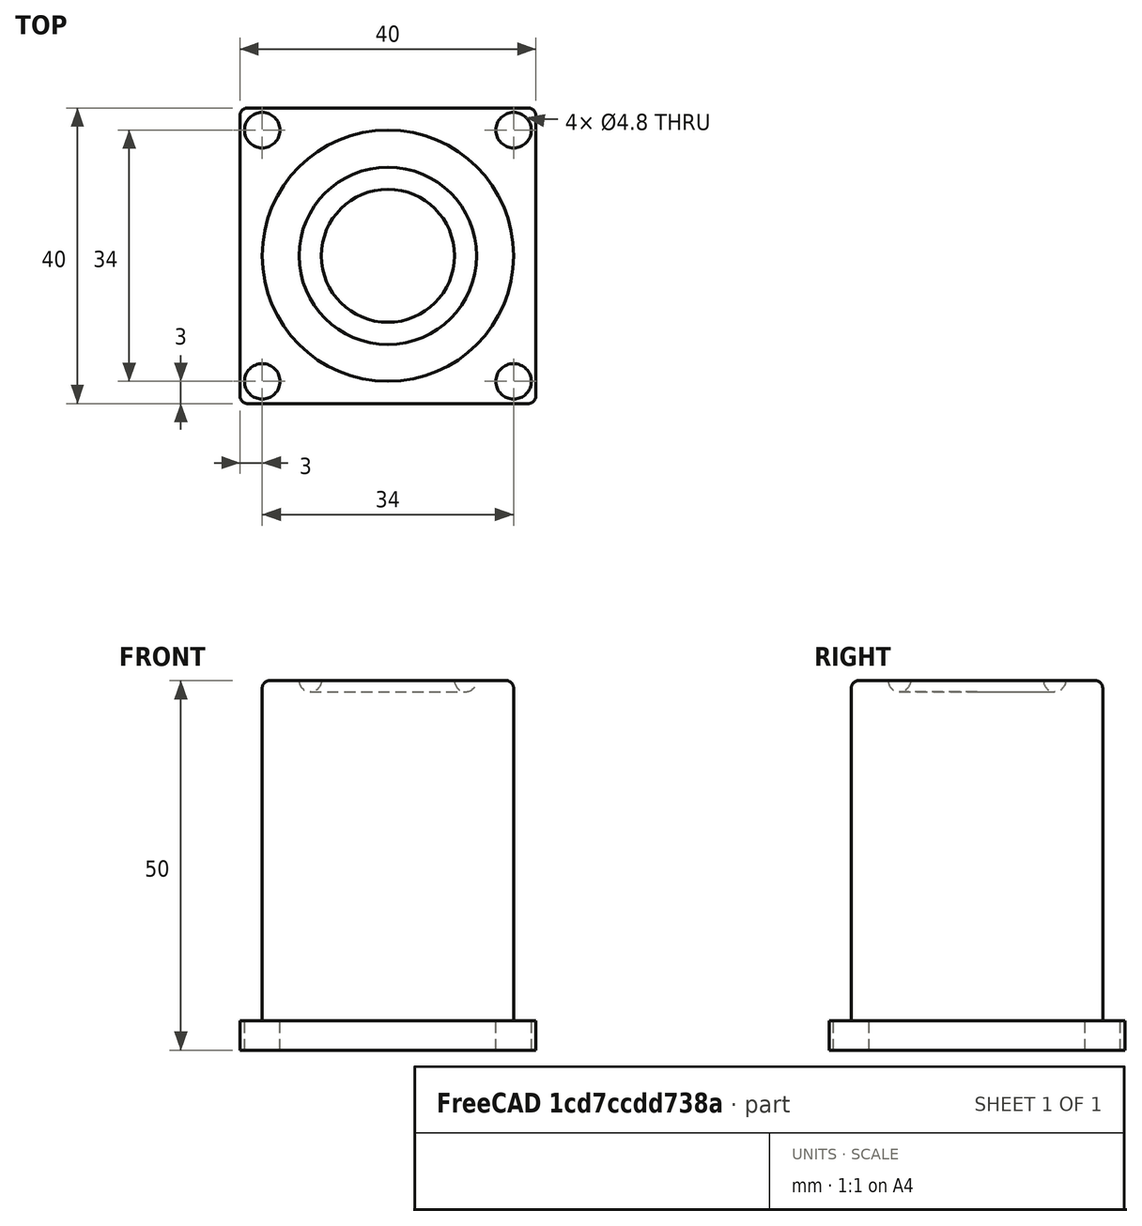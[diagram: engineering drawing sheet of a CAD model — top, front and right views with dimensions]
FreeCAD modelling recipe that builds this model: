
FCSTD DOCUMENT  (FreeCAD 0.16R6707 (Git))
Label: Pata_Ikea
License: CreativeCommons Attribution-ShareAlike
LicenseURL: http://creativecommons.org/licenses/by-sa/4.0/
objects: Part::Cylinder×2, Part::Cut×2, Part::Box×1, Part::MultiFuse×1, Part::Torus×1, Part::FeaturePython×1, Part::Fillet×1
note: 9 computed .brp shape members not serialized (recipe doc carries the construction recipe); baked Part::Feature solids carry a one-line shape summary decoded from their .brp

FEATURE [Part::Box] Box  label="Base"
  Height = 4
  Length = 40
  Width = 40
FEATURE [Part::Cylinder] Cylinder  label="Pata_maciza"
  Angle = 360
  Height = 50
  Placement = pos=(20,20,0) rot=(0,0,1;0rad)
  Radius = 17
FEATURE [Part::MultiFuse] Fusion  label="Pata_Base"
  Shapes = -> [Cylinder,Box]
FEATURE [Part::Torus] Torus  label="Alojamiento_torica"
  Angle1 = -180
  Angle2 = 180
  Angle3 = 360
  Placement = pos=(20,20,50) rot=(0,0,1;0rad)
  Radius1 = 10.5
  Radius2 = 1.5
FEATURE [Part::Cut] Cut  label="Pata-Alojamineto-torica"
  Base = -> Fusion
  Tool = -> Torus
FEATURE [Part::Cylinder] Cylinder001  label="Taladro_base"
  Angle = 360
  Height = 10
  Placement = pos=(3,3,-1) rot=(0,0,1;0rad)
  Radius = 2.4
FEATURE [Part::FeaturePython] Array  label="Taladros"  # Draft array (typed FeaturePython)
  Angle = 360
  ArrayType = 0
  Axis = (0,0,1)
  Base = -> Cylinder001
  Center = (0,0,0)
  Fuse = false
  IntervalAxis = (0,0,0)
  IntervalX = (34,0,0)
  IntervalY = (0,34,0)
  IntervalZ = (0,0,0)
  NumberPolar = 1
  NumberX = 2
  NumberY = 2
  NumberZ = 1
FEATURE [Part::Cut] Cut001  label="Pata_Ikea"
  Base = -> Cut
  Tool = -> Array
FEATURE [Part::Fillet] Fillet  label="Pata_Ikea_Redondeada"
  Base = -> Cut001
  Edges = 5 edges r=1: [Edge1,Edge15,Edge16,Edge19,Edge21]
